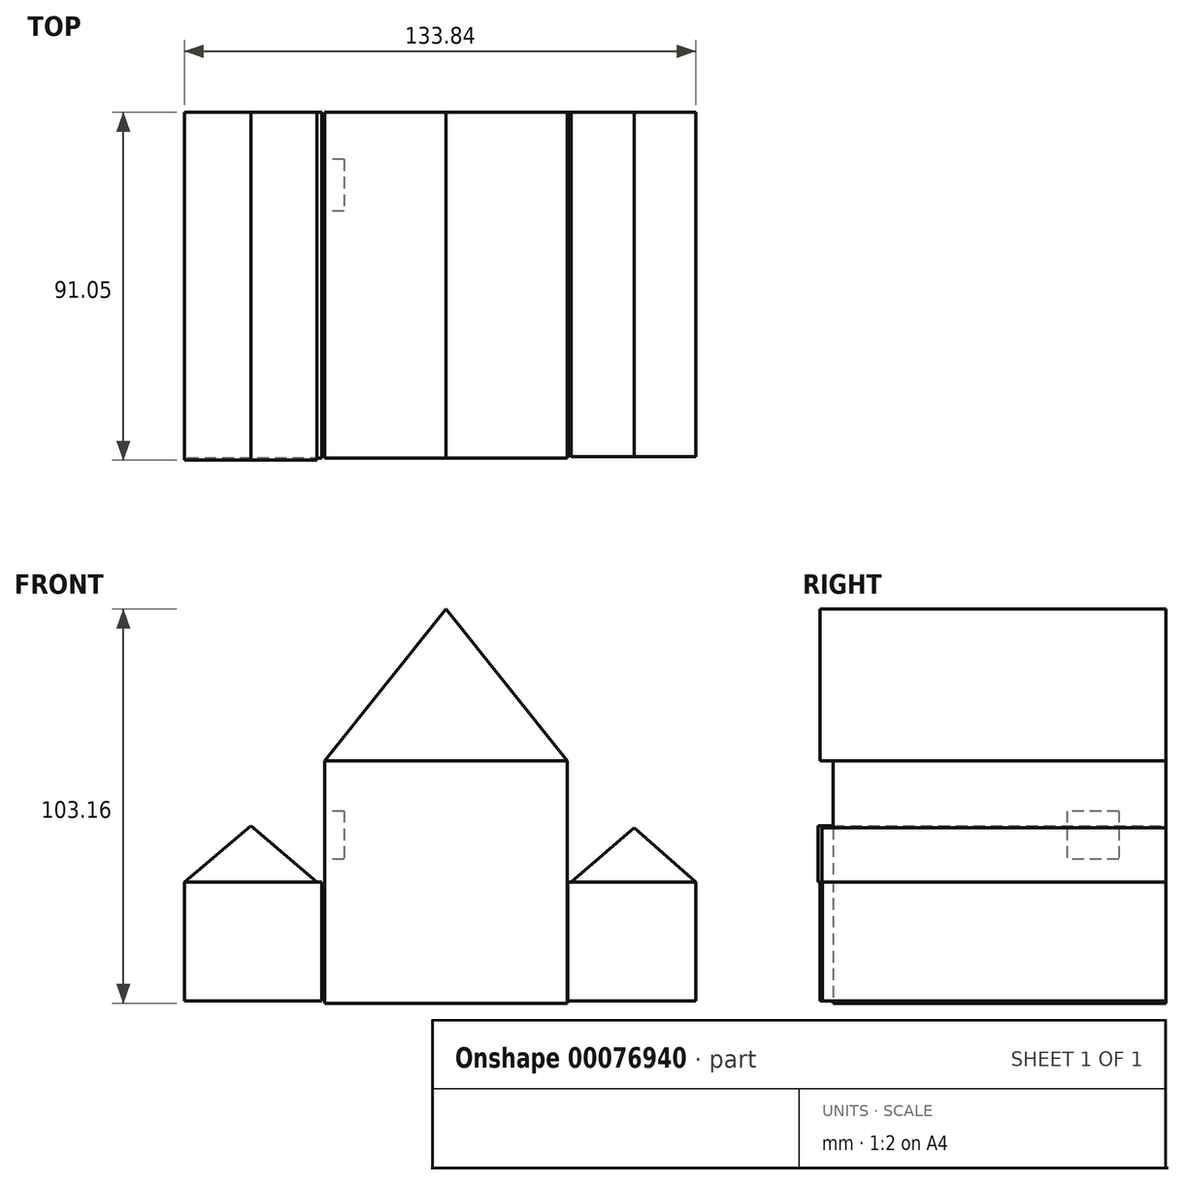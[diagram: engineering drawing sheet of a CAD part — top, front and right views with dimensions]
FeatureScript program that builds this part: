
annotation { "Feature Type Name" : "Feature", "Feature Type Description" : "" }
export const myFeature = defineFeature(function(context is Context, id is Id, definition is map)
    precondition{}
    {
        {
            var Q0;
            Q0=qCreatedBy(makeId("Front.planeOp"),FACE);
            var sketch = newSketch(context, id + "F0", { "sketchPlane" : qUnion([Q0])});
            skLineSegment(sketch, "E0.bottom", {"start": v(31.75, 31.75) * mm, "end": v(-31.75, 31.75) * mm});
            skLineSegment(sketch, "E0.top", {"start": v(31.75, -31.75) * mm, "end": v(-31.75, -31.75) * mm});
            skLineSegment(sketch, "E0.left", {"start": v(31.75, 31.75) * mm, "end": v(31.75, -31.75) * mm});
            skLineSegment(sketch, "E0.right", {"start": v(-31.75, 31.75) * mm, "end": v(-31.75, -31.75) * mm});
            skPoint(sketch, "E0.middle", {"position": v(0, 0) * mm});
            skLineSegment(sketch, "E1", {"start": v(-31.75, 31.75) * mm, "end": v(0, 71.4) * mm});
            skLineSegment(sketch, "E2", {"start": v(0, 71.4) * mm, "end": v(31.75, 31.75) * mm});
            skSolve(sketch);
        }
        {
            var Q0;
            Q0=makeQuery(id+"F0.imprint","IMPRINT",FACE,{"disambiguationData":[TD([[makeQuery(id+"F0.imprint","IMPRINT",EDGE,{"derivedFrom":sQuery(id+"F0.wireOp",EDGE,"E0.bottom")}),-1.0]])]});
            var Q1;
            Q1=makeQuery(id+"F0.imprint","IMPRINT",FACE,{"disambiguationData":[TD([[makeQuery(id+"F0.imprint","IMPRINT",EDGE,{"derivedFrom":sQuery(id+"F0.wireOp",EDGE,"E0.bottom")}),1.0]])]});
            extrude(context, id + "F1", {"entities" : qUnion([Q0, Q1]), "depth" : 90.52 * mm});
        }
        {
            var Q0;
            Q0=makeQuery(id+"F1.opExtrude","CAP_FACE",FACE,{"disambiguationData":[OSD([sQuery(id+"F0.wireOp",EDGE,"E0.top"),sQuery(id+"F0.wireOp",EDGE,"E0.left"),sQuery(id+"F0.wireOp",EDGE,"E0.right"),sQuery(id+"F0.wireOp",EDGE,"E1"),sQuery(id+"F0.wireOp",EDGE,"E2")])],"isStart":false});
            var sketch = newSketch(context, id + "F2", { "sketchPlane" : qUnion([Q0])});
            skLineSegment(sketch, "E3", {"start": v(-31.75, 31.75) * mm, "end": v(31.75, 31.75) * mm});
            skSolve(sketch);
        }
        {
            var Q0;
            Q0=makeQuery(id+"F2.imprint","IMPRINT",FACE,{"disambiguationData":[TD([[makeQuery(id+"F2.imprint","IMPRINT",EDGE,{"derivedFrom":sQuery(id+"F2.wireOp",EDGE,"E3")}),-1.0]])]});
            var sketch = newSketch(context, id + "F3", { "sketchPlane" : qUnion([Q0])});
            skLineSegment(sketch, "E4.bottom", {"start": v(5.15, -30.6) * mm, "end": v(-5.15, -30.6) * mm});
            skLineSegment(sketch, "E4.top", {"start": v(5.15, -9.41) * mm, "end": v(-5.15, -9.41) * mm});
            skLineSegment(sketch, "E4.left", {"start": v(5.15, -30.6) * mm, "end": v(5.15, -9.41) * mm});
            skLineSegment(sketch, "E4.right", {"start": v(-5.15, -30.6) * mm, "end": v(-5.15, -9.41) * mm});
            skPoint(sketch, "E4.middle", {"position": v(0, -20) * mm});
            skSolve(sketch);
        }
        {
            var Q0;
            Q0=makeQuery(id+"F3.imprint","IMPRINT",FACE,{"disambiguationData":[TD([[makeQuery(id+"F3.imprint","IMPRINT",EDGE,{"derivedFrom":sQuery(id+"F3.wireOp",EDGE,"E4.bottom")}),-1.0]])]});
            extrude(context, id + "F4", {"entities" : qUnion([Q0]), "operationType" : NewBodyOperationType.REMOVE, "oppositeDirection" : true, "depth" : 1.27 * mm});
        }
        {
            var Q0;
            Q0=makeQuery(id+"F2.imprint","IMPRINT",FACE,{"disambiguationData":[TD([[makeQuery(id+"F2.imprint","IMPRINT",EDGE,{"derivedFrom":sQuery(id+"F2.wireOp",EDGE,"E3")}),-1.0]])]});
            var sketch = newSketch(context, id + "F5", { "sketchPlane" : qUnion([Q0])});
            skPoint(sketch, "E5", {"position": v(-3.09, -20.6) * mm});
            skSolve(sketch);
        }
        {
            var Q0;
            Q0=makeQuery(id+"F1.opExtrude","SWEPT_FACE",FACE,{"disambiguationData":[OSD([sQuery(id+"F0.wireOp",EDGE,"E0.right")])]});
            var sketch = newSketch(context, id + "F6", { "sketchPlane" : qUnion([Q0])});
            skLineSegment(sketch, "E6.bottom", {"start": v(12.3, 18.53) * mm, "end": v(25.84, 18.53) * mm});
            skLineSegment(sketch, "E6.top", {"start": v(12.3, 5.88) * mm, "end": v(25.84, 5.88) * mm});
            skLineSegment(sketch, "E6.left", {"start": v(12.3, 18.53) * mm, "end": v(12.3, 5.88) * mm});
            skLineSegment(sketch, "E6.right", {"start": v(25.84, 18.53) * mm, "end": v(25.84, 5.88) * mm});
            skLineSegment(sketch, "E7", {"start": v(19.07, 18.53) * mm, "end": v(19.07, 5.88) * mm});
            skLineSegment(sketch, "E8", {"start": v(12.3, 12.2) * mm, "end": v(25.84, 12.2) * mm});
            skSolve(sketch);
        }
        {
            var Q0;
            {var subQ0=sQuery(id+"F6.wireOp",EDGE,"E6.left");var subQ1=sQuery(id+"F6.wireOp",EDGE,"E6.bottom");var subQ2=makeQuery(id+"F6.imprint","INTERSECT",VERTEX,{"derivedFrom":[subQ1,subQ0]});Q0=makeQuery(id+"F6.imprint","IMPRINT",FACE,{"disambiguationData":[TD([[makeQuery(id+"F6.imprint","IMPRINT",EDGE,{"disambiguationData":[TD([[subQ2,-1.0]])],"derivedFrom":subQ1}),-1.0]])]});}
            var Q1;
            {var subQ0=sQuery(id+"F6.wireOp",EDGE,"E6.right");var subQ1=sQuery(id+"F6.wireOp",EDGE,"E6.bottom");var subQ2=makeQuery(id+"F6.imprint","INTERSECT",VERTEX,{"derivedFrom":[subQ1,subQ0]});Q1=makeQuery(id+"F6.imprint","IMPRINT",FACE,{"disambiguationData":[TD([[makeQuery(id+"F6.imprint","IMPRINT",EDGE,{"disambiguationData":[TD([[subQ2,1.0]])],"derivedFrom":subQ1}),-1.0]])]});}
            var Q2;
            {var subQ0=sQuery(id+"F6.wireOp",EDGE,"E6.right");var subQ1=sQuery(id+"F6.wireOp",EDGE,"E6.top");var subQ2=makeQuery(id+"F6.imprint","INTERSECT",VERTEX,{"derivedFrom":[subQ1,subQ0]});Q2=makeQuery(id+"F6.imprint","IMPRINT",FACE,{"disambiguationData":[TD([[makeQuery(id+"F6.imprint","IMPRINT",EDGE,{"disambiguationData":[TD([[subQ2,1.0]])],"derivedFrom":subQ1}),1.0]])]});}
            var Q3;
            {var subQ0=sQuery(id+"F6.wireOp",EDGE,"E6.left");var subQ1=sQuery(id+"F6.wireOp",EDGE,"E6.top");var subQ2=makeQuery(id+"F6.imprint","INTERSECT",VERTEX,{"derivedFrom":[subQ1,subQ0]});Q3=makeQuery(id+"F6.imprint","IMPRINT",FACE,{"disambiguationData":[TD([[makeQuery(id+"F6.imprint","IMPRINT",EDGE,{"disambiguationData":[TD([[subQ2,-1.0]])],"derivedFrom":subQ1}),1.0]])]});}
            var Q4;
            Q4=sQuery(id+"F6.wireOp",EDGE,"E7");
            var Q5;
            Q5=sQuery(id+"F6.wireOp",EDGE,"E8");
            extrude(context, id + "F7", {"entities" : qUnion([Q0, Q1, Q2, Q3]), "operationType" : NewBodyOperationType.REMOVE, "surfaceEntities" : qUnion([Q4, Q5]), "oppositeDirection" : true, "depth" : 5.08 * mm});
        }
        {
            var Q0;
            Q0=qCreatedBy(makeId("Front.planeOp"),FACE);
            var sketch = newSketch(context, id + "F8", { "sketchPlane" : qUnion([Q0])});
            skLineSegment(sketch, "E9.bottom", {"start": v(-32.5, -31.18) * mm, "end": v(-68.4, -31.18) * mm});
            skLineSegment(sketch, "E9.top", {"start": v(-32.5, 0) * mm, "end": v(-68.4, 0) * mm});
            skLineSegment(sketch, "E9.left", {"start": v(-32.5, -31.18) * mm, "end": v(-32.5, 0) * mm});
            skLineSegment(sketch, "E9.right", {"start": v(-68.4, -31.18) * mm, "end": v(-68.4, 0) * mm});
            skSolve(sketch);
        }
        {
            var Q0;
            Q0=makeQuery(id+"F8.imprint","IMPRINT",FACE,{"disambiguationData":[TD([[makeQuery(id+"F8.imprint","IMPRINT",EDGE,{"derivedFrom":sQuery(id+"F8.wireOp",EDGE,"E9.bottom")}),-1.0]])]});
            extrude(context, id + "F9", {"entities" : qUnion([Q0]), "depth" : 90.52 * mm});
        }
        {
            var Q0;
            Q0=qCreatedBy(makeId("Front.planeOp"),FACE);
            var sketch = newSketch(context, id + "F10", { "sketchPlane" : qUnion([Q0])});
            skArc(sketch, "E10", {"start": v(-33.1, 0) * mm, "mid": v(-50.6, 15.22) * mm, "end": v(-68.1, 0) * mm});
            skSolve(sketch);
        }
        {
            var Q0;
            Q0=sQuery(id+"F10.wireOp",EDGE,"E10");
            extrude(context, id + "F11", {"bodyType" : ToolBodyType.SURFACE, "surfaceEntities" : qUnion([Q0]), "depth" : 91.01 * mm});
        }
        {
            var Q0;
            Q0=qCreatedBy(makeId("Front.planeOp"),FACE);
            var sketch = newSketch(context, id + "F12", { "sketchPlane" : qUnion([Q0])});
            skLineSegment(sketch, "E11.bottom", {"start": v(31.92, -31.18) * mm, "end": v(65.45, -31.18) * mm});
            skLineSegment(sketch, "E11.top", {"start": v(31.92, 0) * mm, "end": v(65.45, 0) * mm});
            skLineSegment(sketch, "E11.left", {"start": v(31.92, -31.18) * mm, "end": v(31.92, 0) * mm});
            skLineSegment(sketch, "E11.right", {"start": v(65.45, -31.18) * mm, "end": v(65.45, 0) * mm});
            skSolve(sketch);
        }
        {
            var Q0;
            Q0=makeQuery(id+"F12.imprint","IMPRINT",FACE,{"disambiguationData":[TD([[makeQuery(id+"F12.imprint","IMPRINT",EDGE,{"derivedFrom":sQuery(id+"F12.wireOp",EDGE,"E11.bottom")}),1.0]])]});
            extrude(context, id + "F13", {"entities" : qUnion([Q0]), "operationType" : NewBodyOperationType.ADD, "depth" : 89.9 * mm});
        }
        {
            var Q0;
            Q0=qCreatedBy(makeId("Front.planeOp"),FACE);
            var sketch = newSketch(context, id + "F14", { "sketchPlane" : qUnion([Q0])});
            skArc(sketch, "E12", {"start": v(65.16, 0) * mm, "mid": v(48.39, 13.83) * mm, "end": v(31.62, 0) * mm});
            skSolve(sketch);
        }
        {
            var Q0;
            Q0=sQuery(id+"F14.wireOp",EDGE,"E12");
            extrude(context, id + "F15", {"bodyType" : ToolBodyType.SURFACE, "surfaceEntities" : qUnion([Q0]), "depth" : 90.37 * mm});
        }
        {
            var Q0;
            Q0=qCreatedBy(makeId("Front.planeOp"),FACE);
            var sketch = newSketch(context, id + "F16", { "sketchPlane" : qUnion([Q0])});
            skLineSegment(sketch, "E13", {"start": v(65.45, 0) * mm, "end": v(49.27, 14.12) * mm});
            skLineSegment(sketch, "E14", {"start": v(49.27, 14.12) * mm, "end": v(32.8, 0) * mm});
            skLineSegment(sketch, "E15", {"start": v(32.8, 0) * mm, "end": v(65.45, 0) * mm});
            skSolve(sketch);
        }
        {
            var Q0;
            Q0=makeQuery(id+"F16.imprint","IMPRINT",FACE,{"disambiguationData":[TD([[makeQuery(id+"F16.imprint","IMPRINT",EDGE,{"derivedFrom":sQuery(id+"F16.wireOp",EDGE,"E13")}),1.0]])]});
            extrude(context, id + "F17", {"entities" : qUnion([Q0]), "operationType" : NewBodyOperationType.ADD, "depth" : 90.08 * mm});
        }
        {
            var Q0;
            Q0=qCreatedBy(makeId("Front.planeOp"),FACE);
            var sketch = newSketch(context, id + "F18", { "sketchPlane" : qUnion([Q0])});
            skLineSegment(sketch, "E16", {"start": v(-68.4, 0) * mm, "end": v(-51.04, 14.7) * mm});
            skLineSegment(sketch, "E17", {"start": v(-51.04, 14.7) * mm, "end": v(-33.68, 0) * mm});
            skLineSegment(sketch, "E18", {"start": v(-33.68, 0) * mm, "end": v(-68.4, 0) * mm});
            skSolve(sketch);
        }
        {
            var Q0;
            Q0=makeQuery(id+"F18.imprint","IMPRINT",FACE,{"disambiguationData":[TD([[makeQuery(id+"F18.imprint","IMPRINT",EDGE,{"derivedFrom":sQuery(id+"F18.wireOp",EDGE,"E16")}),-1.0]])]});
            extrude(context, id + "F19", {"entities" : qUnion([Q0]), "operationType" : NewBodyOperationType.ADD, "depth" : 91.05 * mm});
        }
        {
            var Q0;
            Q0=makeQuery(id+"F2.imprint","IMPRINT",FACE,{"disambiguationData":[TD([[makeQuery(id+"F2.imprint","IMPRINT",EDGE,{"derivedFrom":sQuery(id+"F2.wireOp",EDGE,"E3")}),-1.0]])]});
            var sketch = newSketch(context, id + "F20", { "sketchPlane" : qUnion([Q0])});
            skLineSegment(sketch, "E19.bottom", {"start": v(-23.68, 23.24) * mm, "end": v(-10.74, 23.24) * mm});
            skLineSegment(sketch, "E19.top", {"start": v(-23.68, 10.3) * mm, "end": v(-10.74, 10.3) * mm});
            skLineSegment(sketch, "E19.left", {"start": v(-23.68, 23.24) * mm, "end": v(-23.68, 10.3) * mm});
            skLineSegment(sketch, "E19.right", {"start": v(-10.74, 23.24) * mm, "end": v(-10.74, 10.3) * mm});
            skLineSegment(sketch, "E20.bottom", {"start": v(10.74, 22.36) * mm, "end": v(23.97, 22.36) * mm});
            skLineSegment(sketch, "E20.top", {"start": v(10.74, 10) * mm, "end": v(23.97, 10) * mm});
            skLineSegment(sketch, "E20.left", {"start": v(10.74, 22.36) * mm, "end": v(10.74, 10) * mm});
            skLineSegment(sketch, "E20.right", {"start": v(23.97, 22.36) * mm, "end": v(23.97, 10) * mm});
            skSolve(sketch);
        }
        {
            var Q0;
            Q0=sQuery(id+"F20.wireOp",EDGE,"E20.bottom");
            var Q1;
            Q1=sQuery(id+"F20.wireOp",EDGE,"E20.left");
            var Q2;
            Q2=sQuery(id+"F20.wireOp",EDGE,"E20.top");
            var Q3;
            Q3=sQuery(id+"F20.wireOp",EDGE,"E20.right");
            var Q4;
            Q4=sQuery(id+"F20.wireOp",EDGE,"E19.bottom");
            var Q5;
            Q5=sQuery(id+"F20.wireOp",EDGE,"E19.right");
            var Q6;
            Q6=sQuery(id+"F20.wireOp",EDGE,"E19.top");
            var Q7;
            Q7=sQuery(id+"F20.wireOp",EDGE,"E19.left");
            extrude(context, id + "F21", {"bodyType" : ToolBodyType.SURFACE, "surfaceEntities" : qUnion([Q0, Q1, Q2, Q3, Q4, Q5, Q6, Q7]), "oppositeDirection" : true, "depth" : 17.33 * mm});
        }
        {
            var Q0;
            Q0=makeQuery(id+"F2.imprint","IMPRINT",FACE,{"disambiguationData":[TD([[makeQuery(id+"F2.imprint","IMPRINT",EDGE,{"derivedFrom":sQuery(id+"F2.wireOp",EDGE,"E3")}),-1.0]])]});
            extrude(context, id + "F22", {"entities" : qUnion([Q0]), "operationType" : NewBodyOperationType.REMOVE, "oppositeDirection" : true, "depth" : 3.36 * mm});
        }
    });
